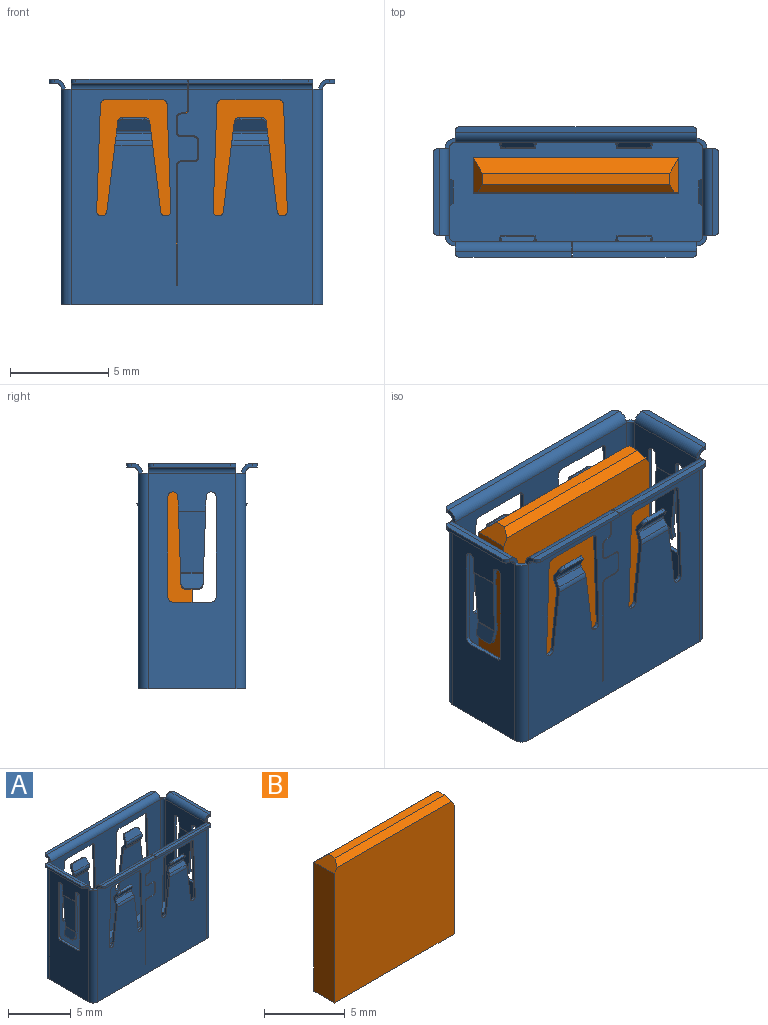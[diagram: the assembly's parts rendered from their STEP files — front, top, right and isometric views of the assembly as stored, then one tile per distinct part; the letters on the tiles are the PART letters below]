
ASSEMBLY  parts=2 mates=1
PART A: 239 faces, bbox 14.5x6.7x11.5 mm
  f0: plane 4.5x0.4mm, normal (0,-1,-0.04), area 0.9mm2, adj f18,f54,f58,f69,f71,f114,f116,f130
  f1: plane 0.2x0.02mm, normal (0,0,1), area 0mm2, adj f24,f39,f155,f203
  f2: cylinder r=0.25mm len=0.25mm, axis (0,-1,0), area 0.1mm2, adj f53,f57,f78,f133
  f3: cylinder r=0.25mm len=0.31mm, axis (0.06,-0.85,-0.52), area 0.1mm2, adj f25,f80,f101,f146
  f4: cylinder r=0.25mm len=0.25mm, axis (0,0,1), area 0.1mm2, adj f8,f12,f32,f147
  f5: cylinder r=0.3mm len=4.47mm, axis (0,-1,0), area 2.1mm2, adj f58,f113,f134,f171
  f6: plane 12.34x0.3mm, normal (0,0,1), area 3.7mm2, adj f48,f90,f103,f105,f112,f170
  f7: cylinder r=0.35mm len=1.81mm, axis (1,0,0), area 0.7mm2, adj f33,f94,f110,f124
  f8: plane 0.55x0.5mm, normal (0,-1,0), area 0.1mm2, adj f4,f12,f32,f40,f83,f172
  f9: plane 4.5x0.4mm, normal (0,1,-0.04), area 0.9mm2, adj f18,f43,f54,f58,f71,f109,f114,f130
  f10: cylinder r=0.3mm len=1.93mm, axis (-1,0,0), area 0.3mm2, adj f53,f78,f85,f199
  f11: plane 2.9x0.2mm, normal (0,0,-1), area 0.6mm2, adj f53,f57,f76,f190
  f12: plane 4.47x0.3mm, normal (0,0,1), area 1.3mm2, adj f4,f8,f140,f147,f172,f182
  f13: cylinder r=0.25mm len=0.31mm, axis (-0.06,0.85,-0.52), area 0.1mm2, adj f37,f132,f148,f196
  f14: plane 5.43x0.2mm, normal (-1,0,-0.03), area 1.1mm2, adj f53,f57,f76,f87
  f15: cylinder r=0.35mm len=1.17mm, axis (0,1,0), area 0.1mm2, adj f21,f120,f212,f214
  f16: cylinder r=0.25mm len=0.31mm, axis (-0.06,-0.85,-0.52), area 0.1mm2, adj f25,f80,f101,f102
  f17: cylinder r=0.15mm len=1.78mm, axis (-1,0,0), area 0.3mm2, adj f47,f80,f102,f146
  f18: cylinder r=0.3mm len=1.39mm, axis (0,1,0), area 0mm2, adj f0,f9,f54,f71
  f19: cylinder r=0.3mm len=1.93mm, axis (-1,0,0), area 0.3mm2, adj f27,f102,f146,f161
  f20: cylinder r=0.25mm len=0.25mm, axis (0,-1,0), area 0.1mm2, adj f155,f161,f164,f165
  f21: plane 1.16x0.75mm, normal (-0.97,0,-0.24), area 0.9mm2, adj f15,f26,f98,f120,f212,f226
  f22: plane 1.96x0.2mm, normal (0,0,1), area 0.4mm2, adj f61,f62,f224,f225
  f23: cylinder r=0.3mm len=12.34mm, axis (-1,0,0), area 5.8mm2, adj f57,f66,f103,f105
  f24: cylinder r=0.25mm len=0.26mm, axis (0,1,0), area 0.1mm2, adj f1,f39,f46,f155
  f25: plane 1.15x0.17mm, normal (0,-0.52,0.85), area 0.2mm2, adj f3,f16,f80,f101
  f26: cylinder r=0.25mm len=0.28mm, axis (-0.97,-0.01,-0.24), area 0.1mm2, adj f21,f98,f120,f213
  f27: plane 1.89x0.33mm, normal (0,0.85,-0.52), area 0.7mm2, adj f19,f102,f111,f146
  f28: cylinder r=0.25mm len=0.25mm, axis (0,1,0), area 0.1mm2, adj f53,f57,f86,f193
  f29: cylinder r=0.25mm len=0.25mm, axis (0,1,0), area 0.1mm2, adj f53,f57,f191,f193
  f30: plane 0.82x0.2mm, normal (-1,0,0), area 0.2mm2, adj f39,f129,f155,f231
  f31: plane 0.55x0.5mm, normal (1,0,0), area 0.1mm2, adj f83,f176,f177,f178,f179,f183
  f32: plane 4.47x0.3mm, normal (0,0,-1), area 1.3mm2, adj f4,f8,f40,f140,f147,f182
  f33: plane 4.6x0.56mm, normal (-0.99,0,0.12), area 0.9mm2, adj f7,f39,f94,f104,f106,f107,f119,f124
  f34: cylinder r=0.15mm len=1.78mm, axis (1,0,0), area 0.3mm2, adj f122,f142,f148,f196
  f35: cylinder r=0.2mm len=0.2mm, axis (0,1,0), area 0.1mm2, adj f82,f155,f161,f163
  f36: cylinder r=0.15mm len=1.78mm, axis (-1,0,0), area 0.3mm2, adj f78,f85,f197,f198
  f37: plane 1.15x0.17mm, normal (0,0.52,0.85), area 0.2mm2, adj f13,f121,f132,f196
  f38: plane 0.5x0.5mm, normal (0,0,1), area 0.1mm2, adj f51,f55,f103,f140
  f39: plane 10x6.92mm, normal (0,1,0), area 54.3mm2, adj f1,f24,f30,f33,f42,f46,f60,f63
  f40: cylinder r=0.3mm len=4.47mm, axis (0,1,0), area 2.1mm2, adj f8,f32,f62,f140
  f41: plane 5.43x0.2mm, normal (1,0,-0.03), area 1.1mm2, adj f70,f155,f161,f187
  f42: plane 0.65x0.2mm, normal (0,0,1), area 0.1mm2, adj f39,f129,f155,f228
  f43: cylinder r=0.25mm len=0.28mm, axis (0.97,-0.01,-0.24), area 0.1mm2, adj f9,f114,f217,f218
  f44: plane 1.15x0.17mm, normal (0,0.52,0.85), area 0.2mm2, adj f45,f144,f197,f201
  f45: plane 1.73x0.58mm, normal (0,-0.85,0.52), area 1.1mm2, adj f44,f78,f85,f144,f200,f201
  f46: plane 5.43x0.2mm, normal (-1,0,-0.03), area 1.1mm2, adj f24,f39,f115,f155
  f47: plane 1.86x0.33mm, normal (0,-0.85,0.52), area 0.7mm2, adj f17,f102,f146,f195
  f48: cylinder r=0.25mm len=0.25mm, axis (0,0,1), area 0.1mm2, adj f6,f66,f103,f170
  f49: cylinder r=0.5mm len=11mm, axis (0,0,1), area 8.6mm2, adj f58,f155,f162,f233
  f50: cylinder r=0.3mm len=10mm, axis (0,0,1), area 4.7mm2, adj f54,f63,f161,f162
  f51: cylinder r=0.3mm len=10mm, axis (0,0,1), area 4.7mm2, adj f38,f53,f61,f63
  f52: cylinder r=0.3mm len=10mm, axis (0,0,1), area 4.7mm2, adj f53,f54,f63,f99
  f53: plane 12.34x10mm, normal (0,-1,0), area 97.9mm2, adj f2,f10,f11,f14,f28,f29,f51,f52
  f54: plane 10x4.47mm, normal (1,0,0), area 32.4mm2, adj f0,f9,f18,f50,f52,f63,f69,f81
  f55: cylinder r=0.5mm len=11mm, axis (0,0,1), area 8.6mm2, adj f38,f57,f62,f233
  f56: cylinder r=0.5mm len=11mm, axis (0,0,1), area 8.6mm2, adj f57,f58,f99,f233
  f57: plane 12.34x11mm, normal (0,1,0), area 110.2mm2, adj f2,f11,f14,f23,f28,f29,f55,f56
  f58: plane 11x4.47mm, normal (-1,0,0), area 36.8mm2, adj f0,f5,f9,f49,f56,f69,f81,f91
  f59: cylinder r=0.5mm len=11mm, axis (0,0,1), area 8.6mm2, adj f62,f83,f155,f233
  f60: cylinder r=0.3mm len=10mm, axis (0,0,1), area 4.7mm2, adj f39,f61,f63,f83
  f61: plane 10x4.47mm, normal (-1,0,0), area 32.4mm2, adj f22,f51,f60,f63,f68,f74,f79,f120
  f62: plane 11x4.47mm, normal (1,0,0), area 36.8mm2, adj f22,f40,f55,f59,f68,f74,f79,f120
  f63: plane 12.94x5.27mm, normal (0,0,1), area 46.6mm2, adj f39,f50,f51,f52,f53,f54,f60,f61
  f64: plane 1.89x0.33mm, normal (0,-0.85,-0.52), area 0.7mm2, adj f92,f97,f122,f148
  f65: cylinder r=0.25mm len=0.26mm, axis (0,1,0), area 0.1mm2, adj f39,f96,f155,f157
  f66: plane 12.34x0.3mm, normal (0,0,-1), area 3.7mm2, adj f23,f48,f103,f105,f112,f170
  f67: plane 0.2x0.13mm, normal (0,0,-1), area 0mm2, adj f72,f155,f161,f232
  f68: cylinder r=0.25mm len=0.25mm, axis (1,0,0), area 0.1mm2, adj f61,f62,f120,f152
  f69: cylinder r=0.25mm len=0.25mm, axis (-1,0,0), area 0.1mm2, adj f0,f54,f58,f208
  f70: cylinder r=0.25mm len=0.26mm, axis (0,-1,0), area 0.1mm2, adj f41,f155,f161,f186
  f71: plane 3.1x1.39mm, normal (1,0,0.06), area 4mm2, adj f0,f9,f18,f145
  f72: cylinder r=0.2mm len=0.2mm, axis (0,1,0), area 0.1mm2, adj f67,f143,f155,f161
  f73: cylinder r=0.25mm len=0.25mm, axis (0,0,1), area 0.1mm2, adj f88,f113,f141,f171
  f74: cylinder r=0.25mm len=0.25mm, axis (1,0,0), area 0.1mm2, adj f61,f62,f152,f210
  f75: cylinder r=0.25mm len=0.25mm, axis (0,1,0), area 0.1mm2, adj f53,f57,f122,f192
  f76: cylinder r=0.25mm len=0.25mm, axis (0,-1,0), area 0.1mm2, adj f11,f14,f53,f57
  f77: cylinder r=0.3mm len=5.95mm, axis (1,0,0), area 2.8mm2, adj f95,f143,f155,f174
  f78: plane 4.6x0.56mm, normal (-0.99,0,0.12), area 0.9mm2, adj f2,f10,f36,f45,f53,f57,f84,f197
  f79: cylinder r=0.25mm len=0.25mm, axis (1,0,0), area 0.1mm2, adj f61,f62,f209,f211
  f80: plane 1.75x0.58mm, normal (0,-0.85,-0.52), area 1.1mm2, adj f3,f16,f17,f25,f102,f146
  f81: cylinder r=0.25mm len=0.25mm, axis (1,0,0), area 0.1mm2, adj f54,f58,f206,f207
  f82: plane 0.82x0.2mm, normal (1,0,0), area 0.2mm2, adj f35,f135,f155,f161
  f83: plane 0.5x0.5mm, normal (0,0,1), area 0.1mm2, adj f8,f31,f59,f60
  f84: cylinder r=0.5mm len=1.93mm, axis (-1,0,0), area 0.5mm2, adj f57,f78,f85,f198
  f85: plane 4.6x0.56mm, normal (0.99,0,0.12), area 0.9mm2, adj f10,f36,f45,f53,f57,f84,f144,f197
  f86: plane 5.43x0.2mm, normal (-1,0,-0.03), area 1.1mm2, adj f28,f53,f57,f149
  f87: cylinder r=0.25mm len=0.26mm, axis (0,-1,0), area 0.1mm2, adj f14,f53,f57,f158
  f88: plane 4.47x0.3mm, normal (0,0,1), area 1.3mm2, adj f73,f125,f134,f141,f171,f181
  f89: plane 5.95x0.3mm, normal (0,0,1), area 1.8mm2, adj f95,f139,f143,f173,f175
  f90: cylinder r=0.5mm len=12.34mm, axis (-1,0,0), area 9.7mm2, adj f6,f53,f103,f105
  f91: plane 5.12x0.2mm, normal (0,1,0), area 1mm2, adj f54,f58,f222,f223
  f92: cylinder r=0.3mm len=1.93mm, axis (1,0,0), area 0.3mm2, adj f53,f64,f122,f148
  f93: plane 2.9x0.2mm, normal (0,0,-1), area 0.6mm2, adj f39,f115,f155,f184
  f94: plane 1.73x0.58mm, normal (0,0.85,0.52), area 1.1mm2, adj f7,f33,f110,f137,f153,f156
  f95: plane 0.55x0.5mm, normal (-1,0,0), area 0.1mm2, adj f77,f89,f139,f162,f173,f174
  f96: plane 5.43x0.2mm, normal (1,0,-0.03), area 1.1mm2, adj f39,f65,f155,f184
  f97: cylinder r=0.35mm len=1.81mm, axis (1,0,0), area 0.7mm2, adj f64,f122,f132,f148
  f98: plane 0.63x0.19mm, normal (0.24,0,-0.97), area 0.1mm2, adj f21,f26,f213,f226
  f99: plane 0.5x0.5mm, normal (0,0,1), area 0.1mm2, adj f52,f56,f105,f134
  f100: plane 2.9x0.2mm, normal (0,0,-1), area 0.6mm2, adj f123,f155,f161,f187
  f101: plane 1.73x0.58mm, normal (0,0.85,0.52), area 1.1mm2, adj f3,f16,f25,f102,f111,f146
  f102: plane 4.6x0.56mm, normal (-0.99,0,0.12), area 0.9mm2, adj f16,f17,f19,f27,f47,f80,f101,f111
  f103: plane 0.55x0.5mm, normal (1,0,0), area 0.1mm2, adj f6,f23,f38,f48,f66,f90
  f104: cylinder r=0.5mm len=1.93mm, axis (1,0,0), area 0.5mm2, adj f33,f110,f138,f155
  f105: plane 0.55x0.5mm, normal (-1,0,0), area 0.1mm2, adj f6,f23,f66,f90,f99,f112
  f106: cylinder r=0.3mm len=1.93mm, axis (1,0,0), area 0.3mm2, adj f33,f39,f110,f124
  f107: plane 1.75x0.58mm, normal (0,-0.85,-0.52), area 1.1mm2, adj f33,f110,f137,f153,f154,f156
  f108: cylinder r=0.25mm len=0.25mm, axis (0,-1,0), area 0.1mm2, adj f39,f155,f168,f169
  f109: cylinder r=0.25mm len=0.25mm, axis (-1,0,0), area 0.1mm2, adj f9,f54,f58,f151
  f110: plane 4.6x0.56mm, normal (0.99,0,0.12), area 0.9mm2, adj f7,f39,f94,f104,f106,f107,f124,f138
  f111: cylinder r=0.35mm len=1.81mm, axis (-1,0,0), area 0.7mm2, adj f27,f101,f102,f146
  f112: cylinder r=0.25mm len=0.25mm, axis (0,0,1), area 0.1mm2, adj f6,f66,f105,f170
  f113: plane 4.47x0.3mm, normal (0,0,-1), area 1.3mm2, adj f5,f73,f134,f141,f171,f181
  f114: plane 1.16x0.75mm, normal (-0.97,0,0.24), area 0.9mm2, adj f0,f9,f43,f116,f217,f220
  f115: cylinder r=0.25mm len=0.25mm, axis (0,1,0), area 0.1mm2, adj f39,f46,f93,f155
  f116: cylinder r=0.25mm len=0.28mm, axis (0.97,0.01,-0.24), area 0.1mm2, adj f0,f114,f217,f218
  f117: cylinder r=0.25mm len=0.25mm, axis (0,1,0), area 0.1mm2, adj f53,f57,f148,f159
  f118: cylinder r=0.15mm len=1.17mm, axis (0,1,0), area 0.1mm2, adj f120,f212,f213,f216
  f119: cylinder r=0.25mm len=0.25mm, axis (0,1,0), area 0.1mm2, adj f33,f39,f155,f157
  f120: plane 4.5x0.4mm, normal (0,1,-0.04), area 0.9mm2, adj f15,f21,f26,f61,f62,f68,f118,f131
  f121: cylinder r=0.25mm len=0.31mm, axis (0.06,0.85,-0.52), area 0.1mm2, adj f37,f122,f132,f196
  f122: plane 4.6x0.56mm, normal (0.99,0,0.12), area 0.9mm2, adj f34,f53,f57,f64,f75,f92,f97,f121
  f123: cylinder r=0.25mm len=0.25mm, axis (0,-1,0), area 0.1mm2, adj f100,f155,f161,f185
  f124: plane 1.89x0.33mm, normal (0,0.85,-0.52), area 0.7mm2, adj f7,f33,f106,f110
  f125: cylinder r=0.5mm len=4.47mm, axis (0,-1,0), area 3.5mm2, adj f54,f88,f134,f171
  f126: plane 0.72x0.2mm, normal (1,0,0), area 0.1mm2, adj f128,f155,f161,f232
  f127: cylinder r=0.5mm len=1.93mm, axis (1,0,0), area 0.5mm2, adj f57,f122,f142,f148
  f128: cylinder r=0.25mm len=0.25mm, axis (0,-1,0), area 0.1mm2, adj f126,f155,f161,f163
  f129: cylinder r=0.25mm len=0.25mm, axis (0,-1,0), area 0.1mm2, adj f30,f39,f42,f155
  f130: cylinder r=0.5mm len=1.39mm, axis (0,1,0), area 0mm2, adj f0,f9,f58,f219
  f131: cylinder r=0.5mm len=1.39mm, axis (0,1,0), area 0mm2, adj f62,f120,f212,f216
  f132: plane 1.73x0.58mm, normal (0,-0.85,0.52), area 1.1mm2, adj f13,f37,f97,f121,f122,f148
  f133: plane 0.2x0.02mm, normal (0,0,1), area 0mm2, adj f2,f53,f57,f150
  f134: plane 0.55x0.5mm, normal (0,1,0), area 0.1mm2, adj f5,f88,f99,f113,f125,f181
  f135: cylinder r=0.2mm len=0.2mm, axis (0,1,0), area 0.1mm2, adj f82,f155,f161,f164
  f136: plane 0.65x0.2mm, normal (0,0,-1), area 0.1mm2, adj f39,f155,f229,f231
  f137: cylinder r=0.25mm len=0.31mm, axis (-0.06,-0.85,-0.52), area 0.1mm2, adj f33,f94,f107,f153
  f138: plane 1.86x0.33mm, normal (0,-0.85,0.52), area 0.7mm2, adj f33,f104,f110,f154
  f139: cylinder r=0.25mm len=0.25mm, axis (0,0,1), area 0.1mm2, adj f89,f95,f174,f175
  f140: plane 0.55x0.5mm, normal (0,1,0), area 0.1mm2, adj f12,f32,f38,f40,f172,f182
  f141: plane 3.97x0.2mm, normal (-1,0,0), area 0.8mm2, adj f73,f88,f113,f181
  f142: plane 1.86x0.33mm, normal (0,0.85,0.52), area 0.7mm2, adj f34,f122,f127,f148
  f143: plane 1.52x0.8mm, normal (1,0,0), area 0.4mm2, adj f72,f77,f89,f155,f161,f173,f174,f175
  f144: cylinder r=0.25mm len=0.31mm, axis (0.06,0.85,-0.52), area 0.1mm2, adj f44,f45,f85,f197
  f145: cylinder r=0.35mm len=1.17mm, axis (0,1,0), area 0.1mm2, adj f0,f9,f71,f218
  f146: plane 4.6x0.56mm, normal (0.99,0,0.12), area 0.9mm2, adj f3,f17,f19,f27,f47,f80,f101,f111
  f147: plane 3.97x0.2mm, normal (1,0,0), area 0.8mm2, adj f4,f12,f32,f182
  f148: plane 4.6x0.56mm, normal (-0.99,0,0.12), area 0.9mm2, adj f13,f34,f53,f57,f64,f92,f97,f117
  f149: cylinder r=0.25mm len=0.26mm, axis (0,1,0), area 0.1mm2, adj f53,f57,f86,f192
  f150: cylinder r=0.25mm len=0.26mm, axis (0,-1,0), area 0.1mm2, adj f53,f57,f133,f189
  f151: plane 0.2x0.01mm, normal (0,0,-1), area 0mm2, adj f54,f58,f109,f221
  f152: plane 0.2x0.01mm, normal (0,0,-1), area 0mm2, adj f61,f62,f68,f74
  f153: plane 1.15x0.17mm, normal (0,-0.52,0.85), area 0.2mm2, adj f94,f107,f137,f156
  f154: cylinder r=0.15mm len=1.78mm, axis (1,0,0), area 0.3mm2, adj f33,f107,f110,f138
  f155: plane 12.34x11mm, normal (0,-1,0), area 109.6mm2, adj f1,f20,f24,f30,f33,f35,f41,f42
  f156: cylinder r=0.25mm len=0.31mm, axis (0.06,-0.85,-0.52), area 0.1mm2, adj f94,f107,f110,f153
  f157: plane 0.2x0.02mm, normal (0,0,1), area 0mm2, adj f39,f65,f119,f155
  f158: plane 0.2x0.02mm, normal (0,0,1), area 0mm2, adj f53,f57,f87,f202
  f159: plane 0.2x0.02mm, normal (0,0,1), area 0mm2, adj f53,f57,f117,f194
  f160: plane 0.2x0.02mm, normal (0,0,1), area 0mm2, adj f155,f161,f188,f204
  f161: plane 10x6.47mm, normal (0,1,0), area 43mm2, adj f19,f20,f35,f41,f50,f63,f67,f70
  f162: plane 0.5x0.5mm, normal (0,0,1), area 0.1mm2, adj f49,f50,f95,f171
  f163: plane 0.65x0.2mm, normal (0,0,1), area 0.1mm2, adj f35,f128,f155,f161
  f164: plane 0.65x0.2mm, normal (0,0,-1), area 0.1mm2, adj f20,f135,f155,f161
  f165: plane 6.09x0.2mm, normal (1,0,0), area 1.2mm2, adj f20,f63,f155,f161
  f166: plane 6.09x0.2mm, normal (-1,0,0), area 1.2mm2, adj f39,f63,f155,f228
  f167: plane 0.72x0.2mm, normal (-1,0,0), area 0.1mm2, adj f39,f155,f229,f230
  f168: plane 0.2x0.13mm, normal (0,0,1), area 0mm2, adj f39,f108,f155,f230
  f169: plane 1.52x0.8mm, normal (-1,0,0), area 0.4mm2, adj f39,f108,f155,f176,f177,f178,f179,f180
  f170: plane 11.84x0.2mm, normal (0,1,0), area 2.4mm2, adj f6,f48,f66,f112
  f171: plane 0.55x0.5mm, normal (0,-1,0), area 0.1mm2, adj f5,f73,f88,f113,f125,f162
  f172: cylinder r=0.5mm len=4.47mm, axis (0,1,0), area 3.5mm2, adj f8,f12,f61,f140
  f173: cylinder r=0.5mm len=5.95mm, axis (1,0,0), area 4.7mm2, adj f89,f95,f143,f161
  f174: plane 5.95x0.3mm, normal (0,0,-1), area 1.8mm2, adj f77,f95,f139,f143,f175
  f175: plane 5.7x0.2mm, normal (0,-1,0), area 1.1mm2, adj f89,f139,f143,f174
  f176: cylinder r=0.5mm len=6.34mm, axis (1,0,0), area 5mm2, adj f31,f39,f169,f178
  f177: cylinder r=0.3mm len=6.34mm, axis (1,0,0), area 3mm2, adj f31,f155,f169,f179
  f178: plane 6.34x0.3mm, normal (0,0,1), area 1.9mm2, adj f31,f169,f176,f180,f183
  f179: plane 6.34x0.3mm, normal (0,0,-1), area 1.9mm2, adj f31,f169,f177,f180,f183
  f180: plane 6.09x0.2mm, normal (0,-1,0), area 1.2mm2, adj f169,f178,f179,f183
  f181: cylinder r=0.25mm len=0.25mm, axis (0,0,1), area 0.1mm2, adj f88,f113,f134,f141
  f182: cylinder r=0.25mm len=0.25mm, axis (0,0,1), area 0.1mm2, adj f12,f32,f140,f147
  f183: cylinder r=0.25mm len=0.25mm, axis (0,0,1), area 0.1mm2, adj f31,f178,f179,f180
  f184: cylinder r=0.25mm len=0.25mm, axis (0,1,0), area 0.1mm2, adj f39,f93,f96,f155
  f185: plane 5.43x0.2mm, normal (-1,0,-0.03), area 1.1mm2, adj f123,f155,f161,f188
  f186: plane 0.2x0.02mm, normal (0,0,1), area 0mm2, adj f70,f155,f161,f205
  f187: cylinder r=0.25mm len=0.25mm, axis (0,-1,0), area 0.1mm2, adj f41,f100,f155,f161
  f188: cylinder r=0.25mm len=0.26mm, axis (0,-1,0), area 0.1mm2, adj f155,f160,f161,f185
  f189: plane 5.43x0.2mm, normal (1,0,-0.03), area 1.1mm2, adj f53,f57,f150,f190
  f190: cylinder r=0.25mm len=0.25mm, axis (0,-1,0), area 0.1mm2, adj f11,f53,f57,f189
  f191: plane 5.43x0.2mm, normal (1,0,-0.03), area 1.1mm2, adj f29,f53,f57,f194
  f192: plane 0.2x0.02mm, normal (0,0,1), area 0mm2, adj f53,f57,f75,f149
  f193: plane 2.9x0.2mm, normal (0,0,-1), area 0.6mm2, adj f28,f29,f53,f57
  f194: cylinder r=0.25mm len=0.26mm, axis (0,1,0), area 0.1mm2, adj f53,f57,f159,f191
  f195: cylinder r=0.5mm len=1.93mm, axis (-1,0,0), area 0.5mm2, adj f47,f102,f146,f155
  f196: plane 1.75x0.58mm, normal (0,0.85,-0.52), area 1.1mm2, adj f13,f34,f37,f121,f122,f148
  f197: plane 1.75x0.58mm, normal (0,0.85,-0.52), area 1.1mm2, adj f36,f44,f78,f85,f144,f201
  f198: plane 1.86x0.33mm, normal (0,0.85,0.52), area 0.7mm2, adj f36,f78,f84,f85
  f199: plane 1.89x0.33mm, normal (0,-0.85,-0.52), area 0.7mm2, adj f10,f78,f85,f200
  f200: cylinder r=0.35mm len=1.81mm, axis (-1,0,0), area 0.7mm2, adj f45,f78,f85,f199
  f201: cylinder r=0.25mm len=0.31mm, axis (-0.06,0.85,-0.52), area 0.1mm2, adj f44,f45,f78,f197
  f202: cylinder r=0.25mm len=0.25mm, axis (0,-1,0), area 0.1mm2, adj f53,f57,f85,f158
  f203: cylinder r=0.25mm len=0.25mm, axis (0,1,0), area 0.1mm2, adj f1,f39,f110,f155
  f204: cylinder r=0.25mm len=0.25mm, axis (0,-1,0), area 0.1mm2, adj f146,f155,f160,f161
  f205: cylinder r=0.25mm len=0.25mm, axis (0,-1,0), area 0.1mm2, adj f102,f155,f161,f186
  f206: plane 1.96x0.2mm, normal (0,0,1), area 0.4mm2, adj f54,f58,f81,f223
  f207: plane 5.12x0.2mm, normal (0,-1,0), area 1mm2, adj f54,f58,f81,f221
  f208: plane 0.2x0.01mm, normal (0,0,-1), area 0mm2, adj f54,f58,f69,f222
  f209: plane 0.2x0.01mm, normal (0,0,-1), area 0mm2, adj f61,f62,f79,f227
  f210: plane 5.12x0.2mm, normal (0,-1,0), area 1mm2, adj f61,f62,f74,f225
  f211: plane 5.12x0.2mm, normal (0,1,0), area 1mm2, adj f61,f62,f79,f224
  f212: plane 4.5x0.4mm, normal (0,-1,-0.04), area 0.9mm2, adj f15,f21,f61,f62,f118,f131,f213,f214
  f213: plane 1.16x0.75mm, normal (0.97,0,0.24), area 0.9mm2, adj f26,f98,f118,f120,f212,f226
  f214: plane 3.1x1.39mm, normal (-1,0,0.06), area 4mm2, adj f15,f120,f212,f215
  f215: cylinder r=0.3mm len=1.39mm, axis (0,1,0), area 0mm2, adj f61,f120,f212,f214
  f216: plane 3.1x1.39mm, normal (1,0,-0.06), area 4mm2, adj f118,f120,f131,f212
  f217: plane 0.63x0.19mm, normal (-0.24,0,-0.97), area 0.1mm2, adj f43,f114,f116,f218
  f218: plane 1.16x0.75mm, normal (0.97,0,-0.24), area 0.9mm2, adj f0,f9,f43,f116,f145,f217
  f219: plane 3.1x1.39mm, normal (-1,0,-0.06), area 4mm2, adj f0,f9,f130,f220
  f220: cylinder r=0.15mm len=1.17mm, axis (0,1,0), area 0.1mm2, adj f0,f9,f114,f219
  f221: cylinder r=0.25mm len=0.25mm, axis (1,0,0), area 0.1mm2, adj f54,f58,f151,f207
  f222: cylinder r=0.25mm len=0.25mm, axis (1,0,0), area 0.1mm2, adj f54,f58,f91,f208
  f223: cylinder r=0.25mm len=0.25mm, axis (1,0,0), area 0.1mm2, adj f54,f58,f91,f206
  f224: cylinder r=0.25mm len=0.25mm, axis (1,0,0), area 0.1mm2, adj f22,f61,f62,f211
  f225: cylinder r=0.25mm len=0.25mm, axis (1,0,0), area 0.1mm2, adj f22,f61,f62,f210
  f226: cylinder r=0.25mm len=0.28mm, axis (-0.97,0.01,-0.24), area 0.1mm2, adj f21,f98,f212,f213
  f227: cylinder r=0.25mm len=0.25mm, axis (1,0,0), area 0.1mm2, adj f61,f62,f209,f212
  f228: cylinder r=0.2mm len=0.2mm, axis (0,1,0), area 0.1mm2, adj f39,f42,f155,f166
  f229: cylinder r=0.2mm len=0.2mm, axis (0,1,0), area 0.1mm2, adj f39,f136,f155,f167
  f230: cylinder r=0.2mm len=0.2mm, axis (0,1,0), area 0.1mm2, adj f39,f155,f167,f168
  f231: cylinder r=0.25mm len=0.25mm, axis (0,-1,0), area 0.1mm2, adj f30,f39,f136,f155
  f232: cylinder r=0.25mm len=0.25mm, axis (0,-1,0), area 0.1mm2, adj f67,f126,f155,f161
  f233: plane 13.34x5.47mm, normal (0,0,-1), area 72.8mm2, adj f49,f55,f56,f57,f58,f59,f62,f155
  f234: plane 10.5x0.5mm, normal (0,1,0), area 5.2mm2, adj f63,f235,f237,f238
  f235: plane 1.8x0.5mm, normal (-1,0,0), area 0.9mm2, adj f63,f234,f236,f238
  f236: plane 10.5x0.5mm, normal (0,-1,0), area 5.2mm2, adj f63,f235,f237,f238
  f237: plane 1.8x0.5mm, normal (1,0,0), area 0.9mm2, adj f63,f234,f236,f238
  f238: plane 10.5x1.8mm, normal (0,0,1), area 18.9mm2, adj f234,f235,f236,f237
PART B: 10 faces, bbox 10.5x1.8x10.6 mm
  f0: plane 10.5x1.8mm, normal (0,0,-1), area 18.9mm2, adj f3,f7,f8,f9
  f1: plane 9.58x0.6mm, normal (0,0,1), area 5.7mm2, adj f2,f4,f5,f6
  f2: plane 1.8x0.8mm, normal (-0.87,0,0.5), area 1.2mm2, adj f1,f3,f4,f6,f9
  f3: plane 9.79x1.8mm, normal (-1,0,0), area 17.6mm2, adj f0,f2,f7,f9
  f4: plane 10.04x0.4mm, normal (0,-0.71,0.71), area 5.5mm2, adj f1,f2,f5,f9
  f5: plane 1.8x0.8mm, normal (0.87,0,0.5), area 1.2mm2, adj f1,f4,f6,f8,f9
  f6: plane 10.5x0.8mm, normal (0,0.71,0.71), area 11.4mm2, adj f1,f2,f5,f7
  f7: plane 10.5x9.79mm, normal (0,1,0), area 102.8mm2, adj f0,f3,f6,f8
  f8: plane 9.79x1.8mm, normal (1,0,0), area 17.6mm2, adj f0,f5,f7,f9
  f9: plane 10.5x10.19mm, normal (0,-1,0), area 106.9mm2, adj f0,f2,f3,f4,f5,f8
PLACE A at identity
PLACE B at identity
MATE fastened B.f0 <-> A.f238  axis (0,0,-1) through (0,0.87,-4.03)mm
